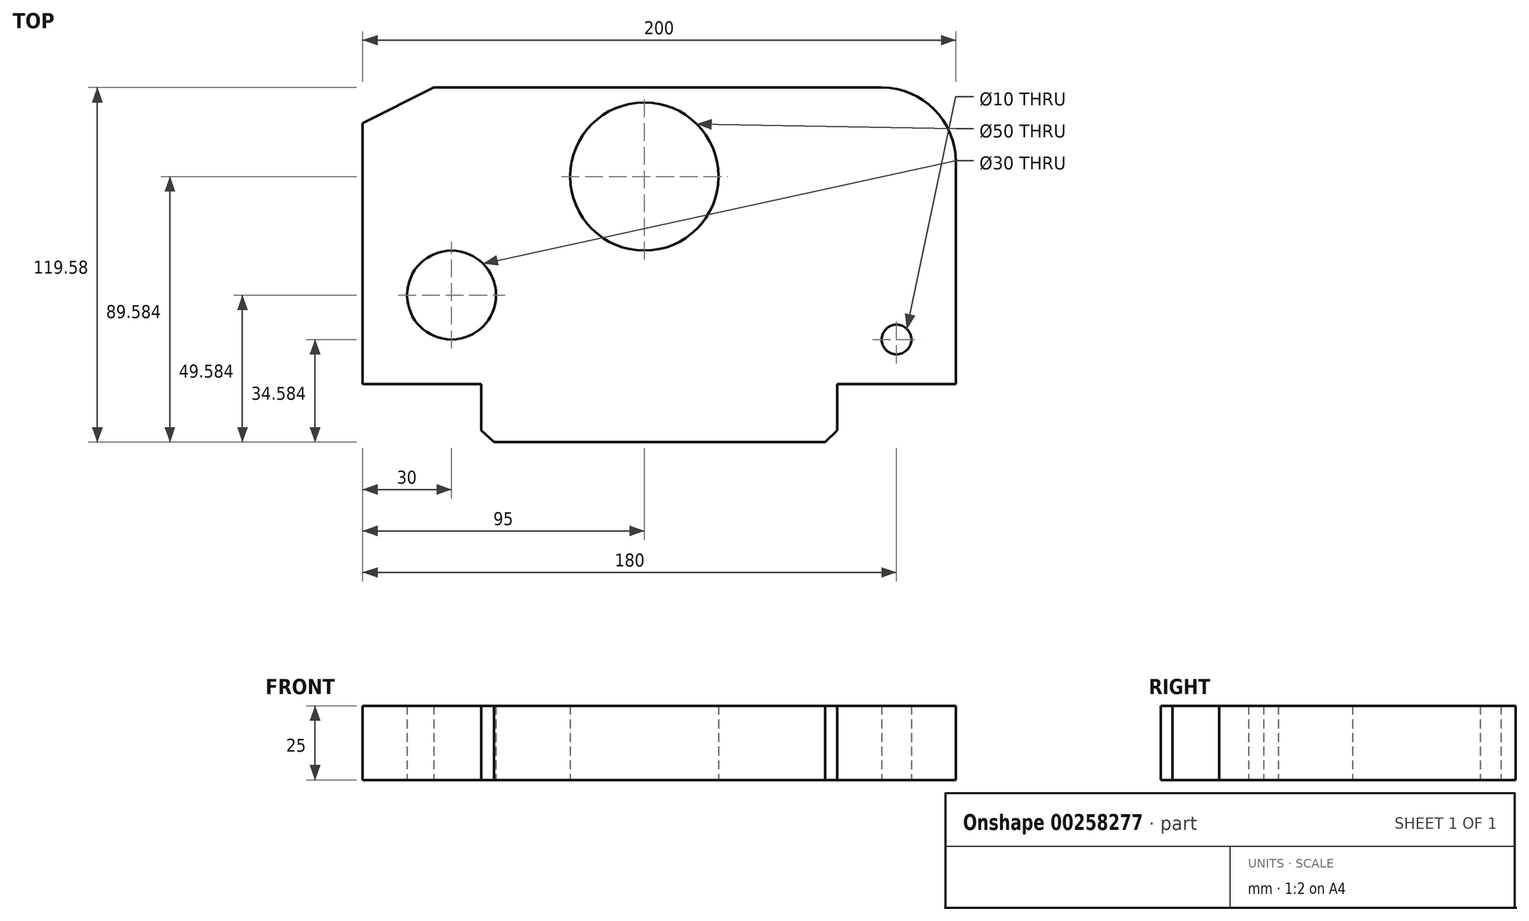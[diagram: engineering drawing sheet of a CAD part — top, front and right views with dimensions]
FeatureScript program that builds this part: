
annotation { "Feature Type Name" : "Feature", "Feature Type Description" : "" }
export const myFeature = defineFeature(function(context is Context, id is Id, definition is map)
    precondition{}
    {
        {
            var Q0;
            Q0=qCreatedBy(makeId("Top.planeOp"),FACE);
            var sketch = newSketch(context, id + "F0", { "sketchPlane" : qUnion([Q0])});
            skLineSegment(sketch, "E0", {"start": v(-70, 46.63) * mm, "end": v(-70, -41.37) * mm});
            skLineSegment(sketch, "E1", {"start": v(-70, 46.63) * mm, "end": v(-46, 58.63) * mm});
            skLineSegment(sketch, "E2", {"start": v(-46, 58.63) * mm, "end": v(105, 58.63) * mm});
            skLineSegment(sketch, "E3", {"start": v(130, 33.63) * mm, "end": v(130, -41.37) * mm});
            skLineSegment(sketch, "E4", {"start": v(-70, -41.37) * mm, "end": v(-30, -41.37) * mm});
            skLineSegment(sketch, "E5", {"start": v(130, -41.37) * mm, "end": v(90, -41.37) * mm});
            skLineSegment(sketch, "E6", {"start": v(-30, -41.37) * mm, "end": v(-30, -57.07) * mm});
            skLineSegment(sketch, "E7", {"start": v(-25.64, -60.95) * mm, "end": v(85.9, -60.95) * mm});
            skLineSegment(sketch, "E8", {"start": v(90, -57.07) * mm, "end": v(90, -41.37) * mm});
            skLineSegment(sketch, "E9", {"start": v(-30, -57.07) * mm, "end": v(-25.64, -60.95) * mm});
            skLineSegment(sketch, "E10", {"start": v(85.9, -60.95) * mm, "end": v(90, -57.07) * mm});
            skLineSegment(sketch, "E11", {"start": v(-70, -41.37) * mm, "end": v(-70, -11.37) * mm});
            skLineSegment(sketch, "E12", {"start": v(-70, -11.37) * mm, "end": v(-40, -11.37) * mm});
            skCircle(sketch, "E13", {"center": v(-40, -11.37) * mm, "radius": 15 * mm});
            skLineSegment(sketch, "E14", {"start": v(-46, 58.63) * mm, "end": v(25, 58.63) * mm});
            skLineSegment(sketch, "E15", {"start": v(25, 58.63) * mm, "end": v(25, 28.63) * mm});
            skCircle(sketch, "E16", {"center": v(25, 28.63) * mm, "radius": 25 * mm});
            skPoint(sketch, "E17.visualSharp", {"position": v(130, 58.63) * mm});
            skArc(sketch, "E17.filletArc", {"start": v(130, 33.63) * mm, "mid": v(122.68, 51.31) * mm, "end": v(105, 58.63) * mm});
            skLineSegment(sketch, "E18", {"start": v(130, -41.37) * mm, "end": v(110, -41.37) * mm});
            skLineSegment(sketch, "E19", {"start": v(110, -41.37) * mm, "end": v(110, -26.37) * mm});
            skCircle(sketch, "E20", {"center": v(110, -26.37) * mm, "radius": 5 * mm});
            skSolve(sketch);
        }
        {
            var Q0;
            Q0 = qSketchRegion(id + "F0", true);
            extrude(context, id + "F1", {"entities" : qUnion([Q0]), "depth" : 25 * mm});
        }
    });
